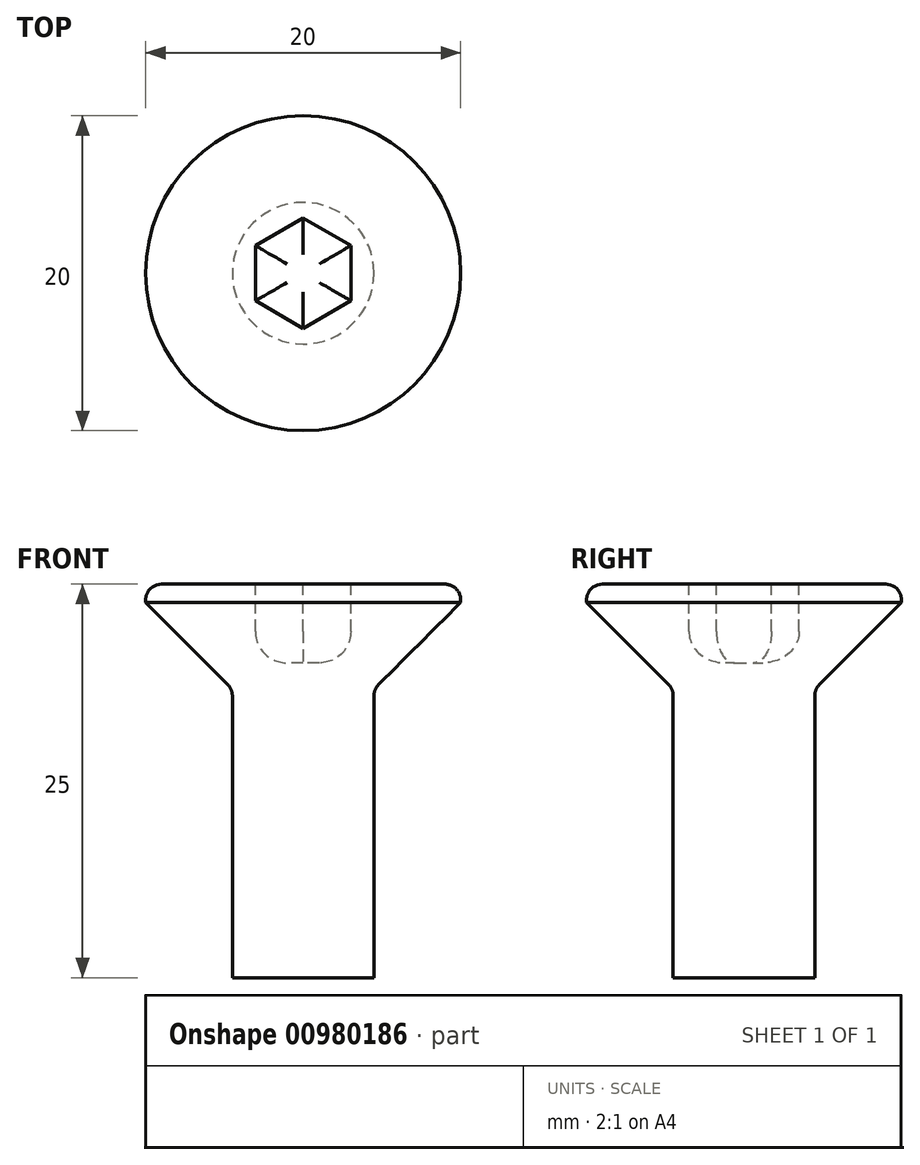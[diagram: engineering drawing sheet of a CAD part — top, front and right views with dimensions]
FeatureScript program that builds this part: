
annotation { "Feature Type Name" : "Feature", "Feature Type Description" : "" }
export const myFeature = defineFeature(function(context is Context, id is Id, definition is map)
    precondition{}
    {
        {
            var Q0;
            Q0=qCreatedBy(makeId("Front.planeOp"),FACE);
            var sketch = newSketch(context, id + "F0", { "sketchPlane" : qUnion([Q0])});
            skLineSegment(sketch, "E0", {"start": v(0, 0) * mm, "end": v(-9, 0) * mm});
            skLineSegment(sketch, "E1", {"start": v(-10, -1) * mm, "end": v(-10, -1.17) * mm});
            skLineSegment(sketch, "E2", {"start": v(-10, -1.17) * mm, "end": v(-4.8, -6.38) * mm});
            skLineSegment(sketch, "E3", {"start": v(-4.5, -25) * mm, "end": v(-4.5, -7.09) * mm});
            skLineSegment(sketch, "E4", {"start": v(-4.5, -25) * mm, "end": v(0, -25) * mm});
            skPoint(sketch, "E5.visualSharp", {"position": v(-10, 0) * mm});
            skArc(sketch, "E5.filletArc", {"start": v(-9, 0) * mm, "mid": v(-9.7, -0.3) * mm, "end": v(-10, -1) * mm});
            skPoint(sketch, "E6.visualSharp", {"position": v(-4.5, -6.67) * mm});
            skArc(sketch, "E6.filletArc", {"start": v(-4.5, -7.09) * mm, "mid": v(-4.57, -6.7) * mm, "end": v(-4.8, -6.38) * mm});
            skLineSegment(sketch, "E7", {"start": v(0, 4.6) * mm, "end": v(0, -27.5) * mm, "construction": true});
            skLineSegment(sketch, "E8", {"start": v(0, 0) * mm, "end": v(0, -25) * mm});
            skSolve(sketch);
        }
        {
            var Q0;
            Q0=makeQuery(id+"F0.imprint","IMPRINT",FACE,{"disambiguationData":[TD([[makeQuery(id+"F0.imprint","IMPRINT",EDGE,{"derivedFrom":sQuery(id+"F0.wireOp",EDGE,"E0")}),1.0]])]});
            var Q1;
            Q1=sQuery(id+"F0.wireOp",EDGE,"E4");
            var Q2;
            Q2=sQuery(id+"F0.wireOp",EDGE,"E0");
            var Q3;
            Q3=sQuery(id+"F0.wireOp",EDGE,"E3");
            var Q4;
            Q4=sQuery(id+"F0.wireOp",EDGE,"E2");
            var Q5;
            Q5=sQuery(id+"F0.wireOp",EDGE,"E5.filletArc");
            var Q6;
            Q6=sQuery(id+"F0.wireOp",EDGE,"E6.filletArc");
            var Q7;
            Q7=sQuery(id+"F0.wireOp",EDGE,"E1");
            var Q8;
            Q8=sQuery(id+"F0.wireOp",EDGE,"E7");
            revolve(context, id + "F1", {"surfaceOperationType" : NewSurfaceOperationType.NEW, "entities" : qUnion([Q0]), "surfaceEntities" : qUnion([Q1, Q2, Q3, Q4, Q5, Q6, Q7]), "axis" : qUnion([Q8]), "revolveType" : RevolveType.FULL});
        }
        {
            var Q0;
            Q0=makeQuery(id+"F1.opRevolve","SWEPT_FACE",FACE,{"disambiguationData":[OSD([sQuery(id+"F0.wireOp",EDGE,"E0")])]});
            var sketch = newSketch(context, id + "F2", { "sketchPlane" : qUnion([Q0])});
            skCircle(sketch, "E9", {"center": v(0, 0) * mm, "radius": 3.5 * mm, "construction": true});
            skLineSegment(sketch, "E10", {"start": v(0, -3.5) * mm, "end": v(3.03, -1.75) * mm});
            skLineSegment(sketch, "E11", {"start": v(3.03, -1.75) * mm, "end": v(3.03, 1.75) * mm});
            skLineSegment(sketch, "E12", {"start": v(3.03, 1.75) * mm, "end": v(0, 3.5) * mm});
            skLineSegment(sketch, "E13", {"start": v(0, 3.5) * mm, "end": v(-3.03, 1.75) * mm});
            skLineSegment(sketch, "E14", {"start": v(-3.03, 1.75) * mm, "end": v(-3.03, -1.75) * mm});
            skLineSegment(sketch, "E15", {"start": v(-3.03, -1.75) * mm, "end": v(0, -3.5) * mm});
            skSolve(sketch);
        }
        {
            var Q0;
            Q0=makeQuery(id+"F2.imprint","IMPRINT",FACE,{"disambiguationData":[TD([[makeQuery(id+"F2.imprint","IMPRINT",EDGE,{"derivedFrom":sQuery(id+"F2.wireOp",EDGE,"E10")}),1.0]])]});
            extrude(context, id + "F3", {"entities" : qUnion([Q0]), "operationType" : NewBodyOperationType.REMOVE, "oppositeDirection" : true, "depth" : 5 * mm, "offsetDistance" : 25 * mm});
        }
        {
            var Q0;
            Q0=makeQuery(id+"F3.boolean.opBoolean","COPY",EDGE,{"derivedFrom":makeQuery(id+"F3.opExtrude","CAP_EDGE",EDGE,{"disambiguationData":[OSD([sQuery(id+"F2.wireOp",EDGE,"E10")])],"isStart":false})});
            var Q1;
            Q1=makeQuery(id+"F3.boolean.opBoolean","COPY",EDGE,{"derivedFrom":makeQuery(id+"F3.opExtrude","CAP_EDGE",EDGE,{"disambiguationData":[OSD([sQuery(id+"F2.wireOp",EDGE,"E11")])],"isStart":false})});
            var Q2;
            Q2=makeQuery(id+"F3.boolean.opBoolean","COPY",EDGE,{"derivedFrom":makeQuery(id+"F3.opExtrude","CAP_EDGE",EDGE,{"disambiguationData":[OSD([sQuery(id+"F2.wireOp",EDGE,"E15")])],"isStart":false})});
            var Q3;
            Q3=makeQuery(id+"F3.boolean.opBoolean","COPY",EDGE,{"derivedFrom":makeQuery(id+"F3.opExtrude","CAP_EDGE",EDGE,{"disambiguationData":[OSD([sQuery(id+"F2.wireOp",EDGE,"E14")])],"isStart":false})});
            var Q4;
            Q4=makeQuery(id+"F3.boolean.opBoolean","COPY",EDGE,{"derivedFrom":makeQuery(id+"F3.opExtrude","CAP_EDGE",EDGE,{"disambiguationData":[OSD([sQuery(id+"F2.wireOp",EDGE,"E13")])],"isStart":false})});
            var Q5;
            Q5=makeQuery(id+"F3.boolean.opBoolean","COPY",EDGE,{"derivedFrom":makeQuery(id+"F3.opExtrude","CAP_EDGE",EDGE,{"disambiguationData":[OSD([sQuery(id+"F2.wireOp",EDGE,"E12")])],"isStart":false})});
            fillet(context, id + "F4", {"entities" : qUnion([Q0, Q1, Q2, Q3, Q4, Q5]), "radius" : 2 * mm, "allowEdgeOverflow" : false});
        }
    });
